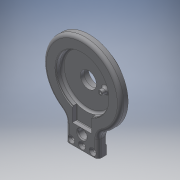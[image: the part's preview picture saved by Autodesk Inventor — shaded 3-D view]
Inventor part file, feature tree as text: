
AUTODESK INVENTOR PART (.ipt)
format: ipt  version: 2019.4 (Build 234330000, 330)  size: 372,224 bytes
history: native  units: mm
features: sketch x17, extrude x15, fillet x7, pattern_circular x2, hole x2, projected_geometry x2, pattern_linear x1, chamfer x1
ambient origin geometry x8: Origin, YZ Plane, XZ Plane, XY Plane, X Axis, Y Axis, Z Axis, Center Point
bodies: Solid1 (feature_tree)
feature tree (47):
  extrude  "Extrusion1"  Depth=72.0mm
  extrude  "Extrusion2"  Depth=54.0mm
  extrude  "Extrusion3"  Depth=1.0mm
  extrude  "Extrusion4"  Depth=18.08mm
  extrude  "Extrusion5"  Depth=8.0mm
  extrude  "Extrusion6"  Depth=1.0mm
  extrude  "Extrusion7"  Depth=5.0mm TaperAngle=0.0deg
  fillet  "Fillet1"  Radius=2.0mm
  extrude  "Extrusion10"  Depth=4.0mm TaperAngle=0.0deg
  pattern_circular  "Circular Pattern1"  Count=8 Angle=360.0deg
  extrude  "Extrusion11"  Depth=54.0mm
  fillet  "Fillet2"  Radius=30.0mm
  extrude  "Extrusion12"  Depth=10.0mm
  extrude  "Extrusion13"  Depth=8.0mm
  hole  "Hole1"  [1 undecoded]
  pattern_linear  "Rectangular Pattern1"  Count1=2 Spacing1=10.0mm
  fillet  "Fillet3"  Radius=10.0mm
  fillet  "Fillet4"  Radius=1.0mm
  extrude  "Extrusion14"  Depth=3.0mm
  extrude  "Extrusion15"  Depth=2.0mm
  fillet  "Fillet5"  Radius=3.5mm
  fillet  "Fillet6"  Radius=1.0mm
  extrude  "Extrusion16"  Depth=2.0mm
  extrude  "Extrusion17"  Depth=2.0mm
  fillet  "Fillet7"  Radius=18.0mm
  hole  "Hole2"  [1 undecoded]
  chamfer  "Chamfer1"  [1 undecoded]
  pattern_circular  "Circular Pattern2"  [2 undecoded]
  sketch  "Sketch1"  dims[d0=50.0mm d1=72.0mm]
  sketch  "Sketch2"  dims[d2=7.0mm d3=0.0mm d4=54.0mm]
  sketch  "Sketch3"  dims[d5=1.0mm d6=0.0mm d7=49.95mm]
  sketch  "Sketch4"  dims[d8=7.0mm d9=0.0mm d10=18.08mm]
  sketch  "Sketch5"  dims[d11=8.0mm d12=0.0mm d13=50.3mm]
  sketch  "Sketch6"  dims[d14=1.0mm d15=0.0mm d16=49.0mm]
  sketch  "Sketch7"  dims[d17=5.0mm d18=0.0mm d20=5.0mm d21=0.0mm d25=2.0mm]
  sketch  "Sketch10"  dims[d29=3.05mm d30=4.0mm d31=0.0mm d32=80.0mm d33=360.0deg]
  sketch  "Sketch11"  dims[d35=30.0mm d36=54.0mm d37=30.0mm]
  sketch  "Sketch12"  dims[d38=3.0mm d39=0.0mm d40=10.0mm]
  sketch  "Sketch13"  dims[d41=8.0mm d42=13.0mm]
  sketch  "Sketch14"  dims[d43=3.0mm d44=0.0mm d45=4.0mm]
  sketch  "Sketch15"  dims[d46=2.0mm]
  sketch  "Sketch16"  dims[d47=16.0mm]
  projected_geometry  "Projected Loop2"
  sketch  "Sketch17"  dims[d48=5.0mm d49=0.0mm]
  sketch  "Sketch18"  dims[d50=6.0mm]
  projected_geometry  "Projected Loop3"
  sketch  "Sketch19"  dims[d51=4.0mm d52=3.1mm d53=6.0mm d54=6.5mm d55=2.0mm d56=90.0deg d57=10.0mm d58=0.0mm d59=20.0mm d61=10.0mm d62=20.0mm d64=10.0mm d65=1.0mm d66=3.0mm d67=15.0mm d68=3.5mm d69=0.0mm d70=1.0mm d71=0.0mm d72=2.0mm d73=2.0mm d74=18.0mm d75=9.0mm d76=0.0mm d77=4.0mm d78=0.0mm d79=10.0mm d80=0.0mm d81=1.0mm d82=28.0mm d83=3.0mm d84=2.459mm d85=15.0mm d86=4.0mm d87=2.0mm d88=90.0deg d89=20.0mm d90=0.0mm d91=0.5mm d92=2.0mm d93=45.0deg d94=30.0mm d95=360.0deg]
note: 5 required parameter values undecoded (feature->parameter linkage not recoverable at this tier; creation-order binding heuristic only, values carry confidence <= 0.55)
